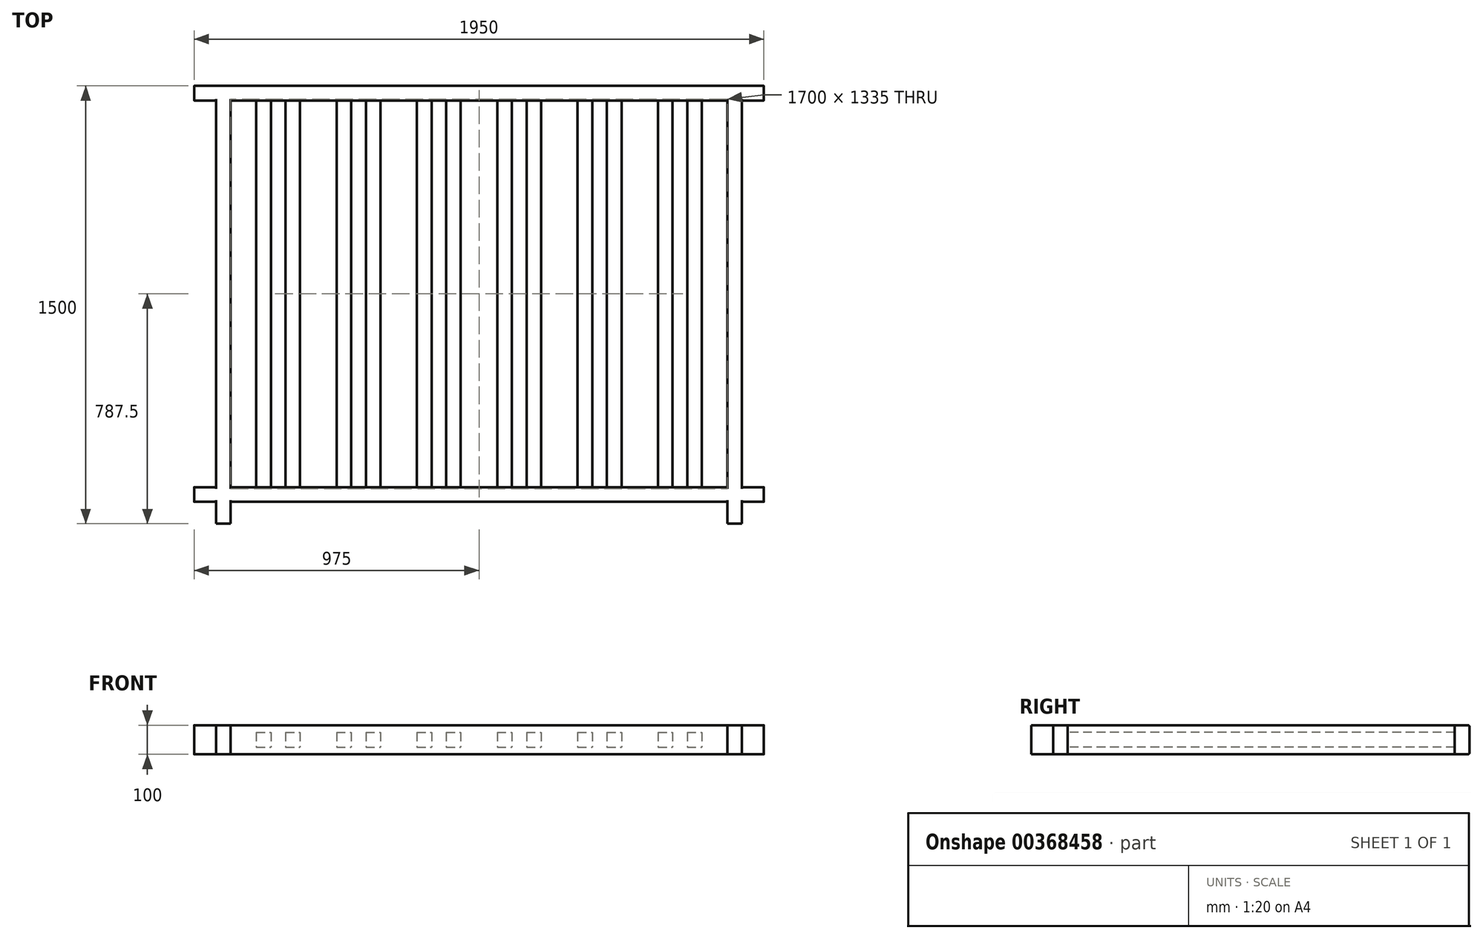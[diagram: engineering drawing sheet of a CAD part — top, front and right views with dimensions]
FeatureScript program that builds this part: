
annotation { "Feature Type Name" : "Feature", "Feature Type Description" : "" }
export const myFeature = defineFeature(function(context is Context, id is Id, definition is map)
    precondition{}
    {
        {
            var Q0;
            Q0=qCreatedBy(makeId("Top.planeOp"),FACE);
            var sketch = newSketch(context, id + "F0", { "sketchPlane" : qUnion([Q0])});
            skLineSegment(sketch, "E0.bottom", {"start": v(0, 0) * mm, "end": v(1950, 0) * mm, "construction": true});
            skLineSegment(sketch, "E0.top", {"start": v(0, 1500) * mm, "end": v(1950, 1500) * mm, "construction": true});
            skLineSegment(sketch, "E0.left", {"start": v(0, 0) * mm, "end": v(0, 1500) * mm, "construction": true});
            skLineSegment(sketch, "E0.right", {"start": v(1950, 0) * mm, "end": v(1950, 1500) * mm, "construction": true});
            skLineSegment(sketch, "E1.bottom", {"start": v(0, 1500) * mm, "end": v(1950, 1500) * mm});
            skLineSegment(sketch, "E1.top", {"start": v(0, 1450) * mm, "end": v(1950, 1450) * mm});
            skLineSegment(sketch, "E1.left", {"start": v(0, 1500) * mm, "end": v(0, 1450) * mm});
            skLineSegment(sketch, "E1.right", {"start": v(1950, 1500) * mm, "end": v(1950, 1450) * mm});
            skLineSegment(sketch, "E2.bottom", {"start": v(0, 125) * mm, "end": v(1950, 125) * mm});
            skLineSegment(sketch, "E2.top", {"start": v(0, 75) * mm, "end": v(1950, 75) * mm});
            skLineSegment(sketch, "E2.left", {"start": v(0, 125) * mm, "end": v(0, 75) * mm});
            skLineSegment(sketch, "E2.right", {"start": v(1950, 125) * mm, "end": v(1950, 75) * mm});
            skLineSegment(sketch, "E3.bottom", {"start": v(75, 1500) * mm, "end": v(125, 1500) * mm});
            skLineSegment(sketch, "E3.top", {"start": v(75, 0) * mm, "end": v(125, 0) * mm});
            skLineSegment(sketch, "E3.left", {"start": v(75, 1500) * mm, "end": v(75, 0) * mm});
            skLineSegment(sketch, "E3.right", {"start": v(125, 1500) * mm, "end": v(125, 0) * mm});
            skLineSegment(sketch, "E4.bottom", {"start": v(1825, 1500) * mm, "end": v(1875, 1500) * mm});
            skLineSegment(sketch, "E4.top", {"start": v(1825, 0) * mm, "end": v(1875, 0) * mm});
            skLineSegment(sketch, "E4.left", {"start": v(1825, 1500) * mm, "end": v(1825, 0) * mm});
            skLineSegment(sketch, "E4.right", {"start": v(1875, 1500) * mm, "end": v(1875, 0) * mm});
            skLineSegment(sketch, "E5", {"start": v(1875, 1450) * mm, "end": v(1875, 125) * mm, "construction": true});
            skLineSegment(sketch, "E6", {"start": v(75, 1450) * mm, "end": v(75, 125) * mm, "construction": true});
            skSolve(sketch);
        }
        {
            var Q0;
            Q0=qSketchRegion(id+"F0",true);
            extrude(context, id + "F1", {"entities" : qUnion([Q0]), "depth" : 75 * mm, "hasSecondDirection" : true, "secondDirectionOppositeDirection" : true, "secondDirectionDepth" : 25 * mm});
        }
        {
            var Q0;
            {var subQ0=sQuery(id+"F0.wireOp",EDGE,"E1.top");Q0=makeQuery(id+"F1.opExtrude","CAP_EDGE",EDGE,{"disambiguationData":[OSD([subQ0]),TDD([makeQuery(id+"F0.imprint","IMPRINT",EDGE,{"disambiguationData":[TD([[makeQuery(id+"F0.imprint","INTERSECT",VERTEX,{"derivedFrom":[subQ0,sQuery(id+"F0.wireOp",EDGE,"E3.right")]}),-1.0]])],"derivedFrom":subQ0})])],"isStart":false});}
            var Q1;
            Q1=makeQuery(id+"F1.opExtrude","CAP_EDGE",EDGE,{"disambiguationData":[OSD([sQuery(id+"F0.wireOp",EDGE,"E1.bottom"),sQuery(id+"F0.wireOp",EDGE,"E3.bottom"),sQuery(id+"F0.wireOp",EDGE,"E4.bottom")])],"isStart":false});
            var Q2;
            {var subQ0=sQuery(id+"F0.wireOp",EDGE,"E2.bottom");Q2=makeQuery(id+"F1.opExtrude","CAP_EDGE",EDGE,{"disambiguationData":[OSD([subQ0]),TDD([makeQuery(id+"F0.imprint","IMPRINT",EDGE,{"disambiguationData":[TD([[makeQuery(id+"F0.imprint","INTERSECT",VERTEX,{"derivedFrom":[subQ0,sQuery(id+"F0.wireOp",EDGE,"E3.right")]}),-1.0]])],"derivedFrom":subQ0})])],"isStart":false});}
            var Q3;
            {var subQ0=sQuery(id+"F0.wireOp",EDGE,"E2.top");Q3=makeQuery(id+"F1.opExtrude","CAP_EDGE",EDGE,{"disambiguationData":[OSD([subQ0]),TDD([makeQuery(id+"F0.imprint","IMPRINT",EDGE,{"disambiguationData":[TD([[makeQuery(id+"F0.imprint","INTERSECT",VERTEX,{"derivedFrom":[subQ0,sQuery(id+"F0.wireOp",EDGE,"E3.right")]}),-1.0]])],"derivedFrom":subQ0})])],"isStart":false});}
            var Q4;
            {var subQ0=sQuery(id+"F0.wireOp",EDGE,"E2.top");Q4=makeQuery(id+"F1.opExtrude","CAP_EDGE",EDGE,{"disambiguationData":[OSD([subQ0]),TDD([makeQuery(id+"F0.imprint","IMPRINT",EDGE,{"disambiguationData":[TD([[makeQuery(id+"F0.imprint","INTERSECT",VERTEX,{"derivedFrom":[subQ0,sQuery(id+"F0.wireOp",EDGE,"E2.left")]}),-1.0]])],"derivedFrom":subQ0})])],"isStart":false});}
            var Q5;
            {var subQ0=sQuery(id+"F0.wireOp",EDGE,"E2.bottom");Q5=makeQuery(id+"F1.opExtrude","CAP_EDGE",EDGE,{"disambiguationData":[OSD([subQ0]),TDD([makeQuery(id+"F0.imprint","IMPRINT",EDGE,{"disambiguationData":[TD([[makeQuery(id+"F0.imprint","INTERSECT",VERTEX,{"derivedFrom":[subQ0,sQuery(id+"F0.wireOp",EDGE,"E2.left")]}),-1.0]])],"derivedFrom":subQ0})])],"isStart":false});}
            var Q6;
            {var subQ0=sQuery(id+"F0.wireOp",EDGE,"E2.bottom");Q6=makeQuery(id+"F1.opExtrude","CAP_EDGE",EDGE,{"disambiguationData":[OSD([subQ0]),TDD([makeQuery(id+"F0.imprint","IMPRINT",EDGE,{"disambiguationData":[TD([[makeQuery(id+"F0.imprint","INTERSECT",VERTEX,{"derivedFrom":[subQ0,sQuery(id+"F0.wireOp",EDGE,"E2.right")]}),1.0]])],"derivedFrom":subQ0})])],"isStart":false});}
            var Q7;
            {var subQ0=sQuery(id+"F0.wireOp",EDGE,"E2.top");Q7=makeQuery(id+"F1.opExtrude","CAP_EDGE",EDGE,{"disambiguationData":[OSD([subQ0]),TDD([makeQuery(id+"F0.imprint","IMPRINT",EDGE,{"disambiguationData":[TD([[makeQuery(id+"F0.imprint","INTERSECT",VERTEX,{"derivedFrom":[subQ0,sQuery(id+"F0.wireOp",EDGE,"E2.right")]}),1.0]])],"derivedFrom":subQ0})])],"isStart":false});}
            var Q8;
            {var subQ0=sQuery(id+"F0.wireOp",EDGE,"E1.top");Q8=makeQuery(id+"F1.opExtrude","CAP_EDGE",EDGE,{"disambiguationData":[OSD([subQ0]),TDD([makeQuery(id+"F0.imprint","IMPRINT",EDGE,{"disambiguationData":[TD([[makeQuery(id+"F0.imprint","INTERSECT",VERTEX,{"derivedFrom":[subQ0,sQuery(id+"F0.wireOp",EDGE,"E1.right")]}),1.0]])],"derivedFrom":subQ0})])],"isStart":false});}
            var Q9;
            {var subQ0=sQuery(id+"F0.wireOp",EDGE,"E1.top");Q9=makeQuery(id+"F1.opExtrude","CAP_EDGE",EDGE,{"disambiguationData":[OSD([subQ0]),TDD([makeQuery(id+"F0.imprint","IMPRINT",EDGE,{"disambiguationData":[TD([[makeQuery(id+"F0.imprint","INTERSECT",VERTEX,{"derivedFrom":[subQ0,sQuery(id+"F0.wireOp",EDGE,"E1.left")]}),-1.0]])],"derivedFrom":subQ0})])],"isStart":false});}
            var Q10;
            Q10=makeQuery(id+"F1.opExtrude","CAP_EDGE",EDGE,{"disambiguationData":[OSD([sQuery(id+"F0.wireOp",EDGE,"E1.bottom"),sQuery(id+"F0.wireOp",EDGE,"E3.bottom"),sQuery(id+"F0.wireOp",EDGE,"E4.bottom")])],"isStart":true});
            var Q11;
            {var subQ0=sQuery(id+"F0.wireOp",EDGE,"E1.top");Q11=makeQuery(id+"F1.opExtrude","CAP_EDGE",EDGE,{"disambiguationData":[OSD([subQ0]),TDD([makeQuery(id+"F0.imprint","IMPRINT",EDGE,{"disambiguationData":[TD([[makeQuery(id+"F0.imprint","INTERSECT",VERTEX,{"derivedFrom":[subQ0,sQuery(id+"F0.wireOp",EDGE,"E3.right")]}),-1.0]])],"derivedFrom":subQ0})])],"isStart":true});}
            var Q12;
            {var subQ0=sQuery(id+"F0.wireOp",EDGE,"E1.top");Q12=makeQuery(id+"F1.opExtrude","CAP_EDGE",EDGE,{"disambiguationData":[OSD([subQ0]),TDD([makeQuery(id+"F0.imprint","IMPRINT",EDGE,{"disambiguationData":[TD([[makeQuery(id+"F0.imprint","INTERSECT",VERTEX,{"derivedFrom":[subQ0,sQuery(id+"F0.wireOp",EDGE,"E1.right")]}),1.0]])],"derivedFrom":subQ0})])],"isStart":true});}
            var Q13;
            {var subQ0=sQuery(id+"F0.wireOp",EDGE,"E2.top");Q13=makeQuery(id+"F1.opExtrude","CAP_EDGE",EDGE,{"disambiguationData":[OSD([subQ0]),TDD([makeQuery(id+"F0.imprint","IMPRINT",EDGE,{"disambiguationData":[TD([[makeQuery(id+"F0.imprint","INTERSECT",VERTEX,{"derivedFrom":[subQ0,sQuery(id+"F0.wireOp",EDGE,"E2.right")]}),1.0]])],"derivedFrom":subQ0})])],"isStart":true});}
            var Q14;
            {var subQ0=sQuery(id+"F0.wireOp",EDGE,"E2.bottom");Q14=makeQuery(id+"F1.opExtrude","CAP_EDGE",EDGE,{"disambiguationData":[OSD([subQ0]),TDD([makeQuery(id+"F0.imprint","IMPRINT",EDGE,{"disambiguationData":[TD([[makeQuery(id+"F0.imprint","INTERSECT",VERTEX,{"derivedFrom":[subQ0,sQuery(id+"F0.wireOp",EDGE,"E2.right")]}),1.0]])],"derivedFrom":subQ0})])],"isStart":true});}
            var Q15;
            {var subQ0=sQuery(id+"F0.wireOp",EDGE,"E2.bottom");Q15=makeQuery(id+"F1.opExtrude","CAP_EDGE",EDGE,{"disambiguationData":[OSD([subQ0]),TDD([makeQuery(id+"F0.imprint","IMPRINT",EDGE,{"disambiguationData":[TD([[makeQuery(id+"F0.imprint","INTERSECT",VERTEX,{"derivedFrom":[subQ0,sQuery(id+"F0.wireOp",EDGE,"E3.right")]}),-1.0]])],"derivedFrom":subQ0})])],"isStart":true});}
            var Q16;
            {var subQ0=sQuery(id+"F0.wireOp",EDGE,"E2.top");Q16=makeQuery(id+"F1.opExtrude","CAP_EDGE",EDGE,{"disambiguationData":[OSD([subQ0]),TDD([makeQuery(id+"F0.imprint","IMPRINT",EDGE,{"disambiguationData":[TD([[makeQuery(id+"F0.imprint","INTERSECT",VERTEX,{"derivedFrom":[subQ0,sQuery(id+"F0.wireOp",EDGE,"E3.right")]}),-1.0]])],"derivedFrom":subQ0})])],"isStart":true});}
            var Q17;
            {var subQ0=sQuery(id+"F0.wireOp",EDGE,"E2.bottom");Q17=makeQuery(id+"F1.opExtrude","CAP_EDGE",EDGE,{"disambiguationData":[OSD([subQ0]),TDD([makeQuery(id+"F0.imprint","IMPRINT",EDGE,{"disambiguationData":[TD([[makeQuery(id+"F0.imprint","INTERSECT",VERTEX,{"derivedFrom":[subQ0,sQuery(id+"F0.wireOp",EDGE,"E2.left")]}),-1.0]])],"derivedFrom":subQ0})])],"isStart":true});}
            var Q18;
            {var subQ0=sQuery(id+"F0.wireOp",EDGE,"E2.top");Q18=makeQuery(id+"F1.opExtrude","CAP_EDGE",EDGE,{"disambiguationData":[OSD([subQ0]),TDD([makeQuery(id+"F0.imprint","IMPRINT",EDGE,{"disambiguationData":[TD([[makeQuery(id+"F0.imprint","INTERSECT",VERTEX,{"derivedFrom":[subQ0,sQuery(id+"F0.wireOp",EDGE,"E2.left")]}),-1.0]])],"derivedFrom":subQ0})])],"isStart":true});}
            var Q19;
            {var subQ0=sQuery(id+"F0.wireOp",EDGE,"E1.top");Q19=makeQuery(id+"F1.opExtrude","CAP_EDGE",EDGE,{"disambiguationData":[OSD([subQ0]),TDD([makeQuery(id+"F0.imprint","IMPRINT",EDGE,{"disambiguationData":[TD([[makeQuery(id+"F0.imprint","INTERSECT",VERTEX,{"derivedFrom":[subQ0,sQuery(id+"F0.wireOp",EDGE,"E1.left")]}),-1.0]])],"derivedFrom":subQ0})])],"isStart":true});}
            fillet(context, id + "F2", {"entities" : qUnion([Q0, Q1, Q2, Q3, Q4, Q5, Q6, Q7, Q8, Q9, Q10, Q11, Q12, Q13, Q14, Q15, Q16, Q17, Q18, Q19]), "radius" : 5 * mm, "tangentPropagation" : true, "allowEdgeOverflow" : false});
        }
        {
            var Q0;
            Q0=qCreatedBy(makeId("Top.planeOp"),FACE);
            var sketch = newSketch(context, id + "F3", { "sketchPlane" : qUnion([Q0])});
            skLineSegment(sketch, "E7.bottom", {"start": v(212.45, 1450) * mm, "end": v(262.45, 1450) * mm});
            skLineSegment(sketch, "E7.top", {"start": v(212.45, 125) * mm, "end": v(262.45, 125) * mm});
            skLineSegment(sketch, "E7.left", {"start": v(212.45, 1450) * mm, "end": v(212.45, 125) * mm});
            skLineSegment(sketch, "E7.right", {"start": v(262.45, 1450) * mm, "end": v(262.45, 125) * mm});
            skLineSegment(sketch, "E8.bottom", {"start": v(312.45, 1450) * mm, "end": v(362.45, 1450) * mm});
            skLineSegment(sketch, "E8.top", {"start": v(312.45, 125) * mm, "end": v(362.45, 125) * mm});
            skLineSegment(sketch, "E8.left", {"start": v(312.45, 1450) * mm, "end": v(312.45, 125) * mm});
            skLineSegment(sketch, "E8.right", {"start": v(362.45, 1450) * mm, "end": v(362.45, 125) * mm});
            skLineSegment(sketch, "E9", {"start": v(262.45, 125) * mm, "end": v(387, 125) * mm, "construction": true});
            skLineSegment(sketch, "E10", {"start": v(262.45, 1450) * mm, "end": v(386.34, 1450) * mm, "construction": true});
            skLineSegment(sketch, "E11.1.0.0", {"start": v(637.45, 1450) * mm, "end": v(637.45, 125) * mm});
            skLineSegment(sketch, "E11.1.0.1", {"start": v(587.45, 1450) * mm, "end": v(587.45, 125) * mm});
            skLineSegment(sketch, "E11.1.0.2", {"start": v(537.45, 1450) * mm, "end": v(537.45, 125) * mm});
            skLineSegment(sketch, "E11.1.0.3", {"start": v(487.45, 1450) * mm, "end": v(487.45, 125) * mm});
            skLineSegment(sketch, "E11.1.0.4", {"start": v(487.45, 125) * mm, "end": v(537.45, 125) * mm});
            skLineSegment(sketch, "E11.1.0.5", {"start": v(487.45, 1450) * mm, "end": v(537.45, 1450) * mm});
            skLineSegment(sketch, "E11.1.0.6", {"start": v(587.45, 125) * mm, "end": v(637.45, 125) * mm});
            skLineSegment(sketch, "E11.1.0.7", {"start": v(587.45, 1450) * mm, "end": v(637.45, 1450) * mm});
            skLineSegment(sketch, "E11.2.0.0", {"start": v(912.45, 1450) * mm, "end": v(912.45, 125) * mm});
            skLineSegment(sketch, "E11.2.0.1", {"start": v(862.45, 1450) * mm, "end": v(862.45, 125) * mm});
            skLineSegment(sketch, "E11.2.0.2", {"start": v(812.45, 1450) * mm, "end": v(812.45, 125) * mm});
            skLineSegment(sketch, "E11.2.0.3", {"start": v(762.45, 1450) * mm, "end": v(762.45, 125) * mm});
            skLineSegment(sketch, "E11.2.0.4", {"start": v(762.45, 125) * mm, "end": v(812.45, 125) * mm});
            skLineSegment(sketch, "E11.2.0.5", {"start": v(762.45, 1450) * mm, "end": v(812.45, 1450) * mm});
            skLineSegment(sketch, "E11.2.0.6", {"start": v(862.45, 125) * mm, "end": v(912.45, 125) * mm});
            skLineSegment(sketch, "E11.2.0.7", {"start": v(862.45, 1450) * mm, "end": v(912.45, 1450) * mm});
            skLineSegment(sketch, "E11.3.0.0", {"start": v(1187.45, 1450) * mm, "end": v(1187.45, 125) * mm});
            skLineSegment(sketch, "E11.3.0.1", {"start": v(1137.45, 1450) * mm, "end": v(1137.45, 125) * mm});
            skLineSegment(sketch, "E11.3.0.2", {"start": v(1087.45, 1450) * mm, "end": v(1087.45, 125) * mm});
            skLineSegment(sketch, "E11.3.0.3", {"start": v(1037.45, 1450) * mm, "end": v(1037.45, 125) * mm});
            skLineSegment(sketch, "E11.3.0.4", {"start": v(1037.45, 125) * mm, "end": v(1087.45, 125) * mm});
            skLineSegment(sketch, "E11.3.0.5", {"start": v(1037.45, 1450) * mm, "end": v(1087.45, 1450) * mm});
            skLineSegment(sketch, "E11.3.0.6", {"start": v(1137.45, 125) * mm, "end": v(1187.45, 125) * mm});
            skLineSegment(sketch, "E11.3.0.7", {"start": v(1137.45, 1450) * mm, "end": v(1187.45, 1450) * mm});
            skLineSegment(sketch, "E11.4.0.0", {"start": v(1462.45, 1450) * mm, "end": v(1462.45, 125) * mm});
            skLineSegment(sketch, "E11.4.0.1", {"start": v(1412.45, 1450) * mm, "end": v(1412.45, 125) * mm});
            skLineSegment(sketch, "E11.4.0.2", {"start": v(1362.45, 1450) * mm, "end": v(1362.45, 125) * mm});
            skLineSegment(sketch, "E11.4.0.3", {"start": v(1312.45, 1450) * mm, "end": v(1312.45, 125) * mm});
            skLineSegment(sketch, "E11.4.0.4", {"start": v(1312.45, 125) * mm, "end": v(1362.45, 125) * mm});
            skLineSegment(sketch, "E11.4.0.5", {"start": v(1312.45, 1450) * mm, "end": v(1362.45, 1450) * mm});
            skLineSegment(sketch, "E11.4.0.6", {"start": v(1412.45, 125) * mm, "end": v(1462.45, 125) * mm});
            skLineSegment(sketch, "E11.4.0.7", {"start": v(1412.45, 1450) * mm, "end": v(1462.45, 1450) * mm});
            skLineSegment(sketch, "E11.5.0.0", {"start": v(1737.45, 1450) * mm, "end": v(1737.45, 125) * mm});
            skLineSegment(sketch, "E11.5.0.1", {"start": v(1687.45, 1450) * mm, "end": v(1687.45, 125) * mm});
            skLineSegment(sketch, "E11.5.0.2", {"start": v(1637.45, 1450) * mm, "end": v(1637.45, 125) * mm});
            skLineSegment(sketch, "E11.5.0.3", {"start": v(1587.45, 1450) * mm, "end": v(1587.45, 125) * mm});
            skLineSegment(sketch, "E11.5.0.4", {"start": v(1587.45, 125) * mm, "end": v(1637.45, 125) * mm});
            skLineSegment(sketch, "E11.5.0.5", {"start": v(1587.45, 1450) * mm, "end": v(1637.45, 1450) * mm});
            skLineSegment(sketch, "E11.5.0.6", {"start": v(1687.45, 125) * mm, "end": v(1737.45, 125) * mm});
            skLineSegment(sketch, "E11.5.0.7", {"start": v(1687.45, 1450) * mm, "end": v(1737.45, 1450) * mm});
            skLineSegment(sketch, "E11.direction1", {"start": v(212.45, 125) * mm, "end": v(487.45, 125) * mm, "construction": true});
            skSolve(sketch);
        }
        {
            var Q0;
            Q0=qSketchRegion(id+"F3",true);
            extrude(context, id + "F4", {"entities" : qUnion([Q0]), "depth" : 50 * mm});
        }
    });
